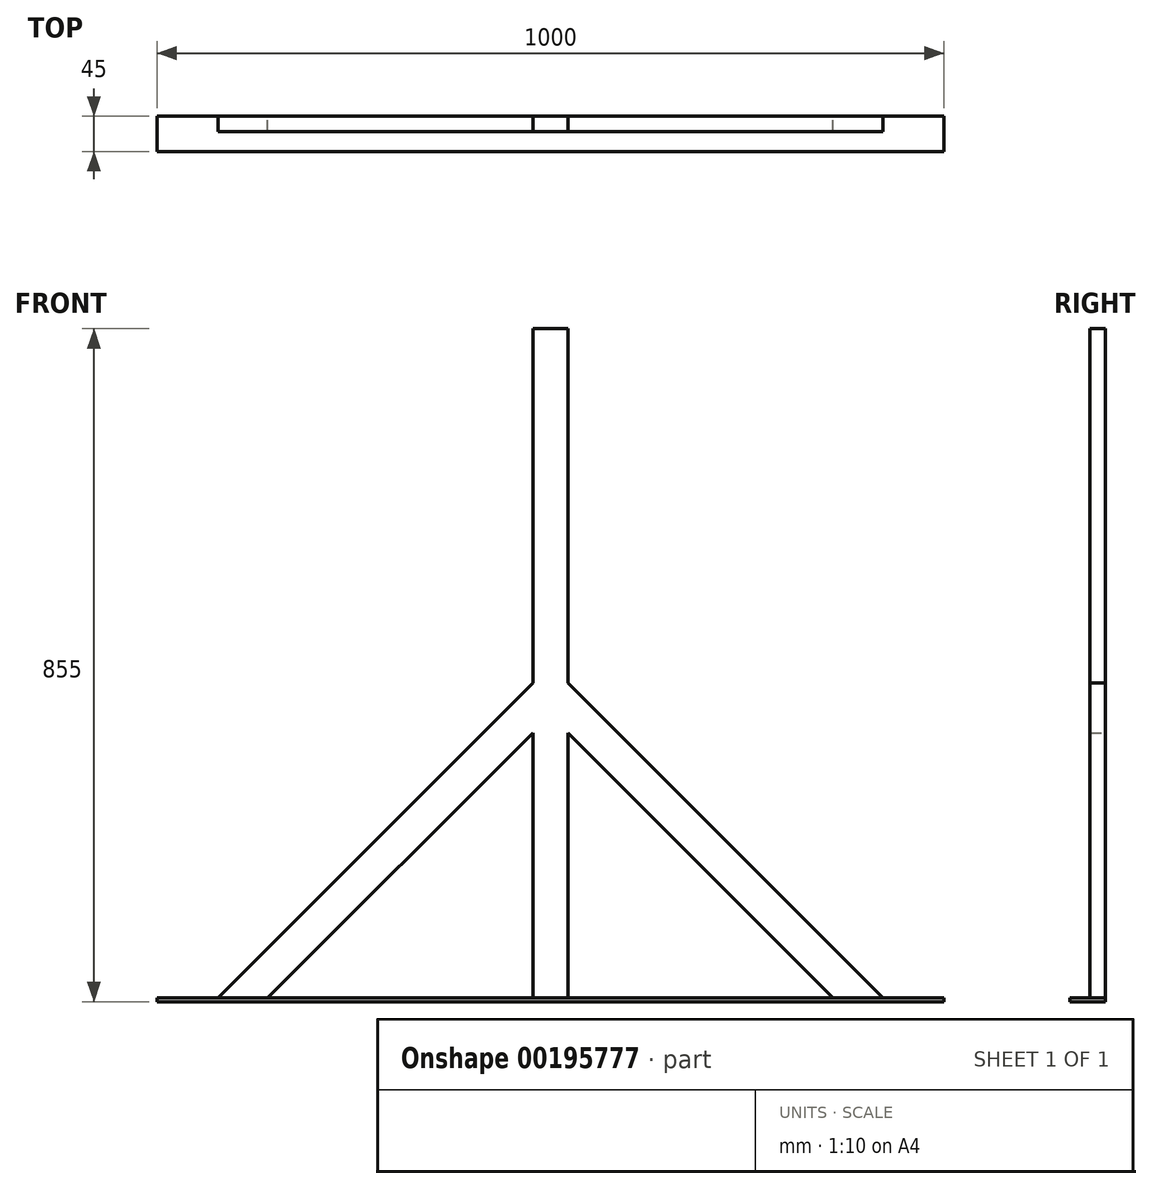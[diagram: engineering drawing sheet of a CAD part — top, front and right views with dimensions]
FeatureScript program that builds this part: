
annotation { "Feature Type Name" : "Feature", "Feature Type Description" : "" }
export const myFeature = defineFeature(function(context is Context, id is Id, definition is map)
    precondition{}
    {
        {
            var Q0;
            Q0=qCreatedBy(makeId("Front.planeOp"),FACE);
            var sketch = newSketch(context, id + "F0", { "sketchPlane" : qUnion([Q0])});
            skLineSegment(sketch, "E0.bottom", {"start": v(500, 2.5) * mm, "end": v(-500, 2.5) * mm});
            skLineSegment(sketch, "E0.top", {"start": v(500, -2.5) * mm, "end": v(-500, -2.5) * mm});
            skLineSegment(sketch, "E0.left", {"start": v(500, 2.5) * mm, "end": v(500, -2.5) * mm});
            skLineSegment(sketch, "E0.right", {"start": v(-500, 2.5) * mm, "end": v(-500, -2.5) * mm});
            skPoint(sketch, "E0.middle", {"position": v(0, 0) * mm});
            skLineSegment(sketch, "E1.bottom", {"start": v(-22.5, 2.5) * mm, "end": v(22.5, 2.5) * mm});
            skLineSegment(sketch, "E1.top", {"start": v(-22.5, 852.5) * mm, "end": v(22.5, 852.5) * mm});
            skLineSegment(sketch, "E1.left", {"start": v(-22.5, 2.5) * mm, "end": v(-22.5, 852.5) * mm});
            skLineSegment(sketch, "E1.right", {"start": v(22.5, 2.5) * mm, "end": v(22.5, 852.5) * mm});
            skPoint(sketch, "E2", {"position": v(-422.5, 2.5) * mm});
            skPoint(sketch, "E3", {"position": v(-22.5, 402.13) * mm});
            skLineSegment(sketch, "E4", {"start": v(-22.5, 402.13) * mm, "end": v(-422.5, 2.5) * mm});
            skLineSegment(sketch, "E5", {"start": v(-22.5, 338.86) * mm, "end": v(-359.17, 2.5) * mm});
            skPoint(sketch, "E6", {"position": v(358.86, 2.5) * mm});
            skPoint(sketch, "E7", {"position": v(22.5, 338.86) * mm});
            skLineSegment(sketch, "E8", {"start": v(22.5, 338.86) * mm, "end": v(358.86, 2.5) * mm});
            skPoint(sketch, "E9", {"position": v(22.5, 402.5) * mm});
            skPoint(sketch, "E10", {"position": v(422.5, 2.5) * mm});
            skLineSegment(sketch, "E11", {"start": v(22.5, 402.5) * mm, "end": v(422.5, 2.5) * mm});
            skSolve(sketch);
        }
        {
            var Q0;
            {var subQ6=sQuery(id+"F0.wireOp",EDGE,"E1.bottom");Q0=makeQuery(id+"F0.imprint","IMPRINT",FACE,{"disambiguationData":[TD([[makeQuery(id+"F0.imprint","IMPRINT",EDGE,{"derivedFrom":subQ6}),1.0]])]});}
            var Q1;
            Q1=makeQuery(id+"F0.imprint","IMPRINT",FACE,{"disambiguationData":[TD([[makeQuery(id+"F0.imprint","IMPRINT",EDGE,{"derivedFrom":sQuery(id+"F0.wireOp",EDGE,"E0.top")}),-1.0]])]});
            extrude(context, id + "F1", {"entities" : qUnion([Q0, Q1]), "depth" : 45 * mm});
        }
        {
            var Q0;
            Q0 = qSketchRegion(id + "F0", true);
            extrude(context, id + "F2", {"entities" : qUnion([Q0]), "operationType" : NewBodyOperationType.ADD, "depth" : 20 * mm});
        }
    });
